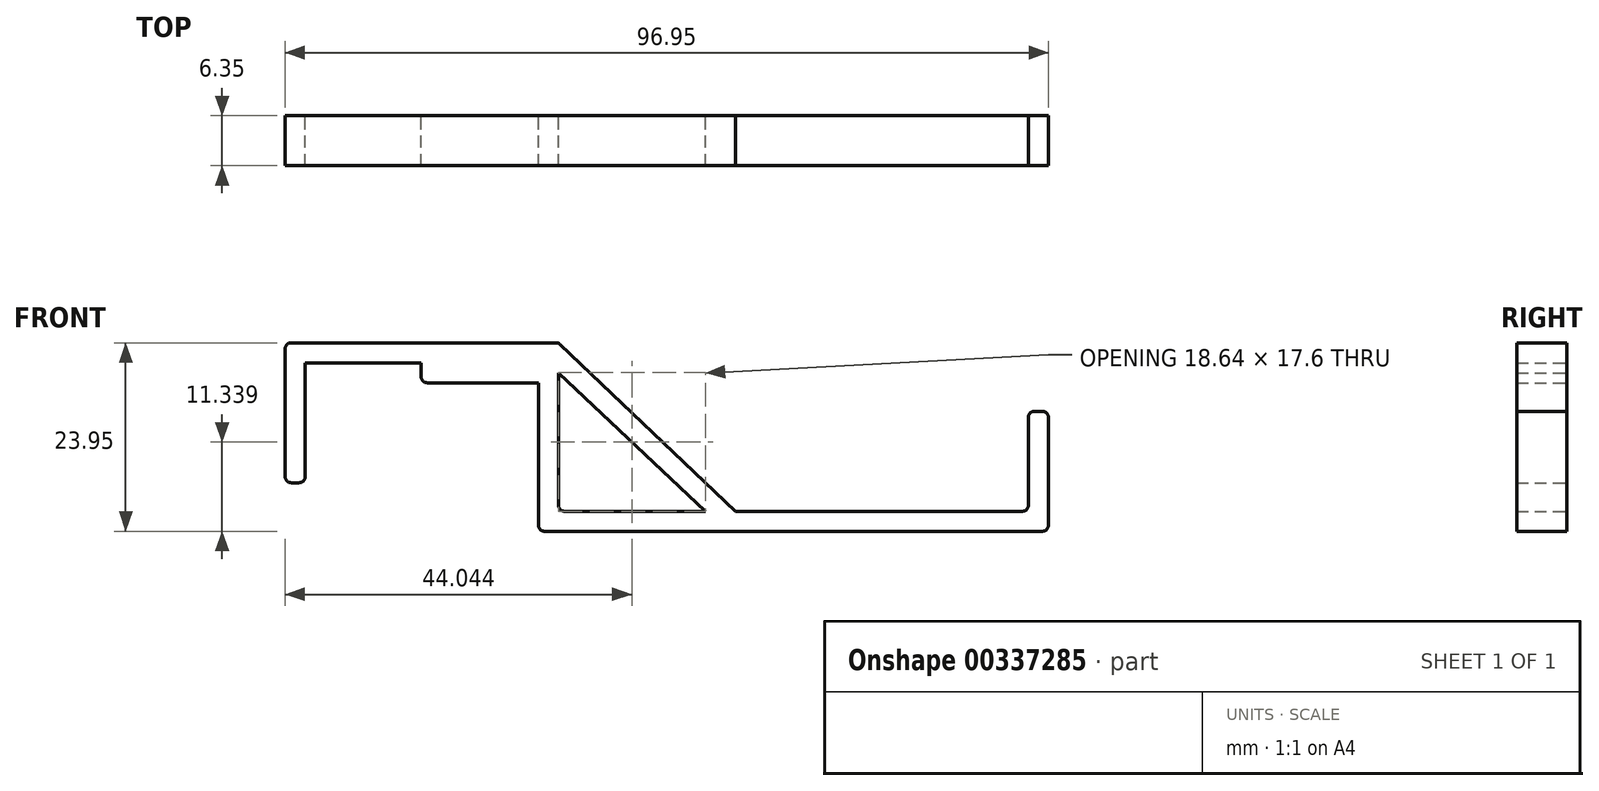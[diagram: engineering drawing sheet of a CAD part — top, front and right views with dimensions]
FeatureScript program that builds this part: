
annotation { "Feature Type Name" : "Feature", "Feature Type Description" : "" }
export const myFeature = defineFeature(function(context is Context, id is Id, definition is map)
    precondition{}
    {
        {
            var Q0;
            Q0=qCreatedBy(makeId("Front.planeOp"),FACE);
            var sketch = newSketch(context, id + "F0", { "sketchPlane" : qUnion([Q0])});
            skLineSegment(sketch, "E0", {"start": v(0, 0) * mm, "end": v(0, -2.54) * mm});
            skLineSegment(sketch, "E1", {"start": v(0, -2.54) * mm, "end": v(29.64, -2.54) * mm});
            skLineSegment(sketch, "E2", {"start": v(14.73, -2.54) * mm, "end": v(14.73, -5.08) * mm});
            skLineSegment(sketch, "E3", {"start": v(0, 0) * mm, "end": v(29.64, 0) * mm});
            skLineSegment(sketch, "E4", {"start": v(14.73, -5.08) * mm, "end": v(29.64, -5.08) * mm});
            skLineSegment(sketch, "E5", {"start": v(29.64, -5.08) * mm, "end": v(29.64, 0) * mm});
            skLineSegment(sketch, "E6", {"start": v(29.64, 0) * mm, "end": v(32.18, 0) * mm});
            skLineSegment(sketch, "E7", {"start": v(32.18, 0) * mm, "end": v(32.18, -23.95) * mm});
            skLineSegment(sketch, "E8", {"start": v(29.64, -5.08) * mm, "end": v(29.64, -23.95) * mm});
            skLineSegment(sketch, "E9", {"start": v(29.64, -23.95) * mm, "end": v(32.18, -23.95) * mm});
            skLineSegment(sketch, "E10", {"start": v(32.18, -23.95) * mm, "end": v(94.41, -23.95) * mm});
            skLineSegment(sketch, "E11", {"start": v(32.18, -21.41) * mm, "end": v(94.41, -21.41) * mm});
            skLineSegment(sketch, "E12", {"start": v(94.41, -21.41) * mm, "end": v(94.41, -23.95) * mm});
            skLineSegment(sketch, "E13", {"start": v(94.41, -21.41) * mm, "end": v(94.41, -8.71) * mm});
            skLineSegment(sketch, "E14", {"start": v(94.41, -8.71) * mm, "end": v(91.87, -8.71) * mm});
            skLineSegment(sketch, "E15", {"start": v(91.87, -8.71) * mm, "end": v(91.87, -21.41) * mm});
            skLineSegment(sketch, "E16", {"start": v(0, 0) * mm, "end": v(-2.54, 0) * mm});
            skLineSegment(sketch, "E17", {"start": v(0, -2.54) * mm, "end": v(0, -17.78) * mm});
            skLineSegment(sketch, "E18", {"start": v(-2.54, 0) * mm, "end": v(-2.54, -17.78) * mm});
            skLineSegment(sketch, "E19", {"start": v(-2.54, -17.78) * mm, "end": v(0, -17.78) * mm});
            skLineSegment(sketch, "E20", {"start": v(32.18, 0) * mm, "end": v(54.64, -21.41) * mm});
            skPoint(sketch, "E21.start.orphan", {"position": v(53.37, 0) * mm});
            skLineSegment(sketch, "E22", {"start": v(32.18, 0) * mm, "end": v(32.18, -3.8) * mm});
            skLineSegment(sketch, "E23", {"start": v(54.64, -21.41) * mm, "end": v(50.83, -21.41) * mm});
            skLineSegment(sketch, "E24", {"start": v(32.18, -3.8) * mm, "end": v(50.83, -21.41) * mm});
            skSolve(sketch);
        }
        {
            var Q0;
            Q0=makeQuery(id+"F0.imprint","IMPRINT",FACE,{"disambiguationData":[TD([[makeQuery(id+"F0.imprint","IMPRINT",EDGE,{"derivedFrom":sQuery(id+"F0.wireOp",EDGE,"E0")}),-1.0]])]});
            var Q1;
            {var subQ5=sQuery(id+"F0.wireOp",EDGE,"E0");Q1=makeQuery(id+"F0.imprint","IMPRINT",FACE,{"disambiguationData":[TD([[makeQuery(id+"F0.imprint","IMPRINT",EDGE,{"derivedFrom":subQ5}),1.0]])]});}
            var Q2;
            {var subQ3=sQuery(id+"F0.wireOp",EDGE,"E2");Q2=makeQuery(id+"F0.imprint","IMPRINT",FACE,{"disambiguationData":[TD([[makeQuery(id+"F0.imprint","IMPRINT",EDGE,{"derivedFrom":subQ3}),1.0]])]});}
            var Q3;
            {var subQ1=sQuery(id+"F0.wireOp",EDGE,"E6");Q3=makeQuery(id+"F0.imprint","IMPRINT",FACE,{"disambiguationData":[TD([[makeQuery(id+"F0.imprint","IMPRINT",EDGE,{"derivedFrom":subQ1}),-1.0]])]});}
            var Q4;
            {var subQ4=sQuery(id+"F0.wireOp",EDGE,"E10");Q4=makeQuery(id+"F0.imprint","IMPRINT",FACE,{"disambiguationData":[TD([[makeQuery(id+"F0.imprint","IMPRINT",EDGE,{"derivedFrom":subQ4}),1.0]])]});}
            var Q5;
            {var subQ0=sQuery(id+"F0.wireOp",EDGE,"E13");Q5=makeQuery(id+"F0.imprint","IMPRINT",FACE,{"disambiguationData":[TD([[makeQuery(id+"F0.imprint","IMPRINT",EDGE,{"derivedFrom":subQ0}),1.0]])]});}
            var Q6;
            {var subQ0=sQuery(id+"F0.wireOp",EDGE,"E20");Q6=makeQuery(id+"F0.imprint","IMPRINT",FACE,{"disambiguationData":[TD([[makeQuery(id+"F0.imprint","IMPRINT",EDGE,{"derivedFrom":subQ0}),-1.0]])]});}
            extrude(context, id + "F1", {"entities" : qUnion([Q0, Q1, Q2, Q3, Q4, Q5, Q6]), "depth" : 6.35 * mm, "offsetDistance" : 25.4 * mm});
        }
        {
            var Q0;
            Q0=makeQuery(id+"F1.opExtrude","SWEPT_EDGE",EDGE,{"disambiguationData":[OSD([sQuery(id+"F0.wireOp",EDGE,"E18"),sQuery(id+"F0.wireOp",EDGE,"E19")])]});
            var Q1;
            Q1=makeQuery(id+"F1.opExtrude","SWEPT_EDGE",EDGE,{"disambiguationData":[OSD([sQuery(id+"F0.wireOp",EDGE,"E17"),sQuery(id+"F0.wireOp",EDGE,"E19")])]});
            var Q2;
            Q2=makeQuery(id+"F1.opExtrude","SWEPT_EDGE",EDGE,{"disambiguationData":[OSD([sQuery(id+"F0.wireOp",EDGE,"E16"),sQuery(id+"F0.wireOp",EDGE,"E18")])]});
            var Q3;
            Q3=makeQuery(id+"F1.opExtrude","SWEPT_EDGE",EDGE,{"disambiguationData":[OSD([sQuery(id+"F0.wireOp",EDGE,"E6"),sQuery(id+"F0.wireOp",EDGE,"E7")])]});
            var Q4;
            Q4=makeQuery(id+"F1.opExtrude","SWEPT_EDGE",EDGE,{"disambiguationData":[OSD([sQuery(id+"F0.wireOp",EDGE,"E7"),sQuery(id+"F0.wireOp",EDGE,"E11")])]});
            var Q5;
            Q5=makeQuery(id+"F1.opExtrude","SWEPT_EDGE",EDGE,{"disambiguationData":[OSD([sQuery(id+"F0.wireOp",EDGE,"E2"),sQuery(id+"F0.wireOp",EDGE,"E4")])]});
            var Q6;
            Q6=makeQuery(id+"F1.opExtrude","SWEPT_EDGE",EDGE,{"disambiguationData":[OSD([sQuery(id+"F0.wireOp",EDGE,"E8"),sQuery(id+"F0.wireOp",EDGE,"E9")])]});
            var Q7;
            Q7=makeQuery(id+"F1.opExtrude","SWEPT_EDGE",EDGE,{"disambiguationData":[OSD([sQuery(id+"F0.wireOp",EDGE,"E10"),sQuery(id+"F0.wireOp",EDGE,"E12")])]});
            var Q8;
            Q8=makeQuery(id+"F1.opExtrude","SWEPT_EDGE",EDGE,{"disambiguationData":[OSD([sQuery(id+"F0.wireOp",EDGE,"E13"),sQuery(id+"F0.wireOp",EDGE,"E14")])]});
            var Q9;
            Q9=makeQuery(id+"F1.opExtrude","SWEPT_EDGE",EDGE,{"disambiguationData":[OSD([sQuery(id+"F0.wireOp",EDGE,"E14"),sQuery(id+"F0.wireOp",EDGE,"E15")])]});
            var Q10;
            Q10=makeQuery(id+"F1.opExtrude","SWEPT_EDGE",EDGE,{"disambiguationData":[OSD([sQuery(id+"F0.wireOp",EDGE,"E11"),sQuery(id+"F0.wireOp",EDGE,"E15")])]});
            fillet(context, id + "F2", {"entities" : qUnion([Q0, Q1, Q2, Q3, Q4, Q5, Q6, Q7, Q8, Q9, Q10]), "radius" : 0.76 * mm, "tangentPropagation" : true, "allowEdgeOverflow" : false});
        }
    });
